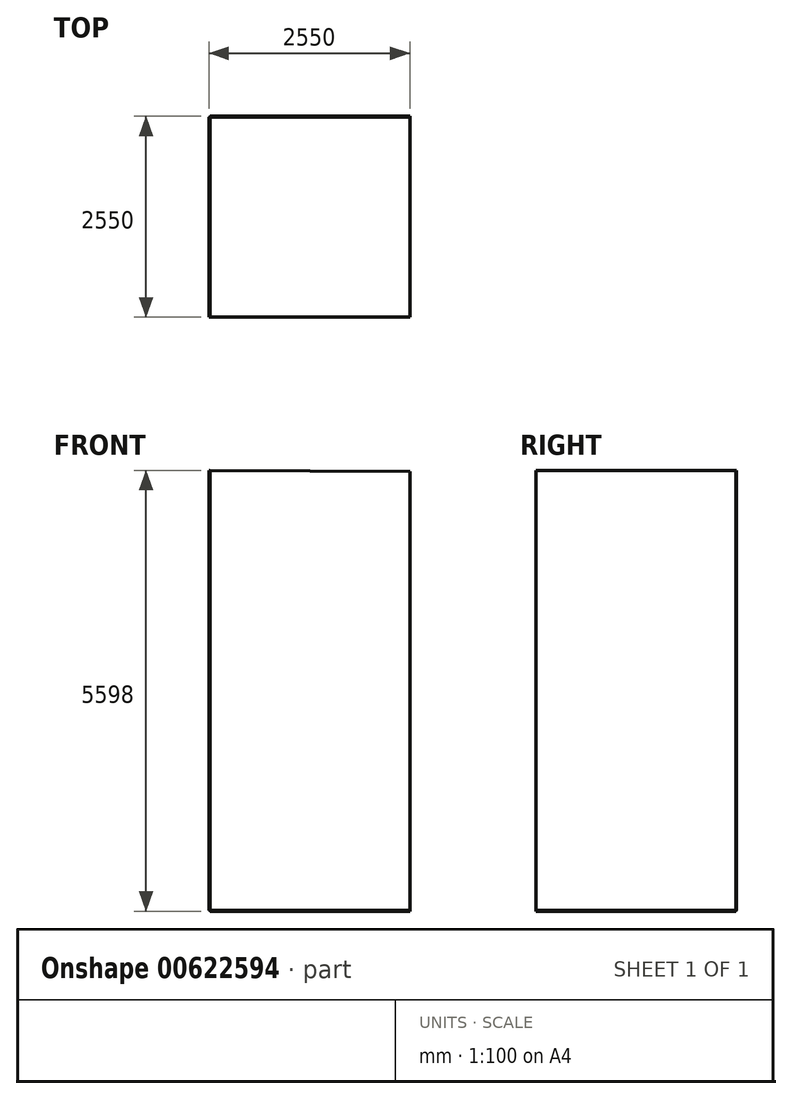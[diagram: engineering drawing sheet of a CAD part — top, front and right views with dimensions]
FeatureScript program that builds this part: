
annotation { "Feature Type Name" : "Feature", "Feature Type Description" : "" }
export const myFeature = defineFeature(function(context is Context, id is Id, definition is map)
    precondition{}
    {
        {
            var Q0;
            Q0=qCreatedBy(makeId("Top.planeOp"),FACE);
            var sketch = newSketch(context, id + "F0", { "sketchPlane" : qUnion([Q0])});
            skLineSegment(sketch, "E0.bottom", {"start": v(0, 0) * mm, "end": v(2540, 0) * mm});
            skLineSegment(sketch, "E0.top", {"start": v(0, 2540) * mm, "end": v(2540, 2540) * mm});
            skLineSegment(sketch, "E0.left", {"start": v(0, 0) * mm, "end": v(0, 2540) * mm});
            skLineSegment(sketch, "E0.right", {"start": v(2540, 0) * mm, "end": v(2540, 2540) * mm});
            skSolve(sketch);
        }
        {
            var Q0;
            Q0=makeQuery(id+"F0.imprint","IMPRINT",FACE,{"disambiguationData":[TD([[makeQuery(id+"F0.imprint","IMPRINT",EDGE,{"derivedFrom":sQuery(id+"F0.wireOp",EDGE,"E0.bottom")}),1.0]])]});
            extrude(context, id + "F1", {"entities" : qUnion([Q0]), "depth" : 10 * mm, "offsetDistance" : 25.4 * mm});
        }
        {
            var Q0;
            Q0=makeQuery(id+"F1.opExtrude","SWEPT_FACE",FACE,{"disambiguationData":[OSD([sQuery(id+"F0.wireOp",EDGE,"E0.left")])]});
            var sketch = newSketch(context, id + "F2", { "sketchPlane" : qUnion([Q0])});
            skLineSegment(sketch, "E1", {"start": v(-2540, 10) * mm, "end": v(0, 10) * mm});
            skLineSegment(sketch, "E2", {"start": v(0, 10) * mm, "end": v(0, 5598) * mm});
            skLineSegment(sketch, "E3", {"start": v(0, 5598) * mm, "end": v(-2540, 5598) * mm});
            skLineSegment(sketch, "E4", {"start": v(-2540, 5598) * mm, "end": v(-2540, 10) * mm});
            skSolve(sketch);
        }
        {
            var Q0;
            Q0=makeQuery(id+"F2.imprint","IMPRINT",FACE,{"disambiguationData":[TD([[makeQuery(id+"F2.imprint","IMPRINT",EDGE,{"derivedFrom":sQuery(id+"F2.wireOp",EDGE,"E1")}),-1.0]])]});
            extrude(context, id + "F3", {"entities" : qUnion([Q0]), "depth" : 10 * mm, "offsetDistance" : 25.4 * mm});
        }
        {
            var Q0;
            Q0=makeQuery(id+"F1.opExtrude","SWEPT_FACE",FACE,{"disambiguationData":[OSD([sQuery(id+"F0.wireOp",EDGE,"E0.top")])]});
            var sketch = newSketch(context, id + "F4", { "sketchPlane" : qUnion([Q0])});
            skLineSegment(sketch, "E5.0", {"start": v(0, 10) * mm, "end": v(-2540, 10) * mm});
            skLineSegment(sketch, "E6.0", {"start": v(0, 5598) * mm, "end": v(0, 10) * mm});
            skLineSegment(sketch, "E7", {"start": v(-2540, 0) * mm, "end": v(-2539.98, 5588) * mm});
            skLineSegment(sketch, "E8", {"start": v(-2539.98, 5588) * mm, "end": v(0, 5598) * mm});
            skSolve(sketch);
        }
        {
            var Q0;
            {var subQ0=sQuery(id+"F4.wireOp",EDGE,"E5.0");Q0=makeQuery(id+"F4.imprint","IMPRINT",FACE,{"disambiguationData":[TD([[makeQuery(id+"F4.imprint","IMPRINT",EDGE,{"derivedFrom":subQ0}),-1.0]])]});}
            extrude(context, id + "F5", {"entities" : qUnion([Q0]), "depth" : 10 * mm, "offsetDistance" : 25.4 * mm});
        }
    });
